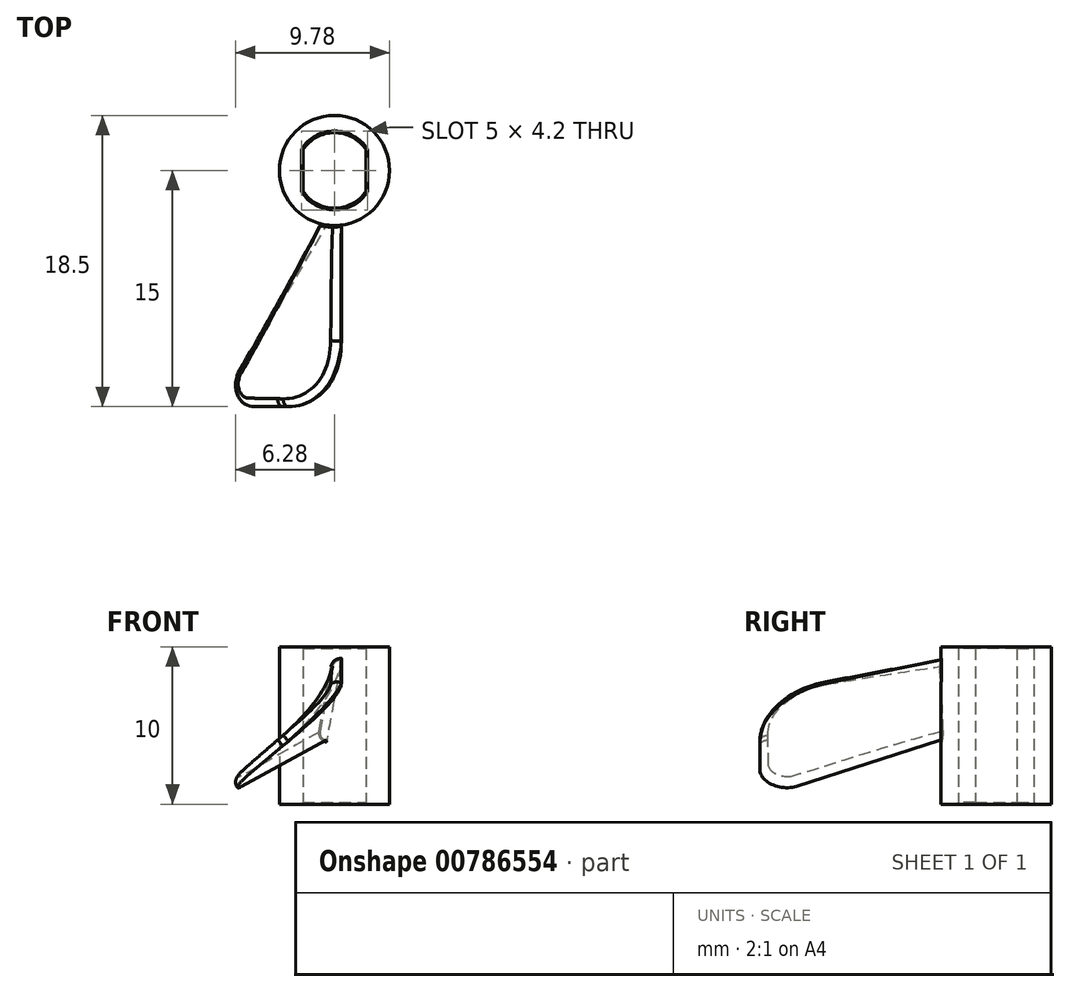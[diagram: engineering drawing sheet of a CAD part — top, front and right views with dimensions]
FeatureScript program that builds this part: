
annotation { "Feature Type Name" : "Feature", "Feature Type Description" : "" }
export const myFeature = defineFeature(function(context is Context, id is Id, definition is map)
    precondition{}
    {
        {
            var Q0;
            Q0=qCreatedBy(makeId("Top.planeOp"),FACE);
            var sketch = newSketch(context, id + "F0", { "sketchPlane" : qUnion([Q0])});
            skCircle(sketch, "E0", {"center": v(0, 0) * mm, "radius": 2.4 * mm});
            skLineSegment(sketch, "E1", {"start": v(-2, 1.33) * mm, "end": v(2, 1.33) * mm});
            skLineSegment(sketch, "E2", {"start": v(-2, -1.33) * mm, "end": v(2, -1.33) * mm});
            skLineSegment(sketch, "E3", {"start": v(-2, 1.33) * mm, "end": v(-2, -1.33) * mm});
            skLineSegment(sketch, "E4", {"start": v(2, 1.33) * mm, "end": v(2, -1.33) * mm});
            skCircle(sketch, "E5", {"center": v(0, 0) * mm, "radius": 3.5 * mm});
            skSolve(sketch);
        }
        {
            var Q0;
            Q0=makeQuery(id+"F0.imprint","IMPRINT",FACE,{"disambiguationData":[TD([[makeQuery(id+"F0.imprint","IMPRINT",EDGE,{"derivedFrom":sQuery(id+"F0.wireOp",EDGE,"E5")}),1.0]])]});
            var Q1;
            {var subQ0=sQuery(id+"F0.wireOp",EDGE,"E4");Q1=makeQuery(id+"F0.imprint","IMPRINT",FACE,{"disambiguationData":[TD([[makeQuery(id+"F0.imprint","IMPRINT",EDGE,{"derivedFrom":subQ0}),1.0]])]});}
            var Q2;
            {var subQ0=sQuery(id+"F0.wireOp",EDGE,"E3");Q2=makeQuery(id+"F0.imprint","IMPRINT",FACE,{"disambiguationData":[TD([[makeQuery(id+"F0.imprint","IMPRINT",EDGE,{"derivedFrom":subQ0}),-1.0]])]});}
            extrude(context, id + "F1", {"entities" : qUnion([Q0, Q1, Q2]), "depth" : 10 * mm, "offsetDistance" : 25 * mm});
        }
        {
            var Q0;
            Q0=qCreatedBy(makeId("Front.planeOp"),FACE);
            cPlane(context, id + "F2", {"entities" : qUnion([Q0]), "cplaneType" : CPlaneType.OFFSET, "offset" : 15 * mm, "width" : 150 * mm, "height" : 150 * mm});
        }
        {
            var Q0;
            Q0=qCreatedBy(id+"F2.planeOp",FACE);
            var sketch = newSketch(context, id + "F3", { "sketchPlane" : qUnion([Q0])});
            skLineSegment(sketch, "E6", {"start": v(-7.23, 10) * mm, "end": v(-7.23, 0) * mm, "construction": true});
            skLineSegment(sketch, "E7", {"start": v(-7.23, 0.38) * mm, "end": v(0.43, 6.81) * mm});
            skLineSegment(sketch, "E8", {"start": v(0.43, 6.81) * mm, "end": v(0.1, 7.2) * mm});
            skLineSegment(sketch, "E9", {"start": v(0.1, 7.2) * mm, "end": v(-7.55, 0.77) * mm});
            skLineSegment(sketch, "E10", {"start": v(-7.55, 0.77) * mm, "end": v(-7.23, 0.38) * mm});
            skSolve(sketch);
        }
        {
            var Q0;
            Q0=qCreatedBy(makeId("Front.planeOp"),FACE);
            cPlane(context, id + "F4", {"entities" : qUnion([Q0]), "cplaneType" : CPlaneType.OFFSET, "offset" : 2.6 * mm, "width" : 150 * mm, "height" : 150 * mm});
        }
        {
            var Q0;
            Q0=qCreatedBy(id+"F4.planeOp",FACE);
            var sketch = newSketch(context, id + "F5", { "sketchPlane" : qUnion([Q0])});
            skLineSegment(sketch, "E11", {"start": v(-0.48, 0) * mm, "end": v(-0.48, 9) * mm, "construction": true});
            skLineSegment(sketch, "E12", {"start": v(-0.48, 4.4) * mm, "end": v(-0.04, 9.39) * mm});
            skLineSegment(sketch, "E13", {"start": v(-0.04, 9.39) * mm, "end": v(0.45, 9.35) * mm});
            skLineSegment(sketch, "E14", {"start": v(0.45, 9.35) * mm, "end": v(0.02, 4.37) * mm});
            skLineSegment(sketch, "E15", {"start": v(0.02, 4.37) * mm, "end": v(-0.48, 4.4) * mm});
            skSolve(sketch);
        }
        {
            var Q1;
            Q1=qSketchRegion(id+"F3",true);
            var Q2;
            Q2=qSketchRegion(id+"F5",true);
            loft(context, id + "F6", {"operationType" : NewBodyOperationType.ADD, "sheetProfilesArray" : [{ "sheetProfileEntities" : qUnion([Q1]) }, { "sheetProfileEntities" : qUnion([Q2]) }]});
        }
        {
            var Q0;
            Q0=makeQuery(id+"F26cwcx8InL0C1a_1.2.F6.opLoft","MID_CAP_EDGE",EDGE,{"disambiguationData":[OSD([sQuery(id+"F3.wireOp",EDGE,"E7"),sQuery(id+"F3.wireOp",EDGE,"E8"),sQuery(id+"F3.wireOp",EDGE,"E9")])],"capPos":0.0});
            var Q1;
            Q1=makeQuery(id+"F6.opLoft","MID_CAP_EDGE",EDGE,{"disambiguationData":[OSD([sQuery(id+"F3.wireOp",EDGE,"E7"),sQuery(id+"F3.wireOp",EDGE,"E8"),sQuery(id+"F3.wireOp",EDGE,"E9")])],"capPos":0.0});
            var Q2;
            Q2=makeQuery(id+"F26cwcx8InL0C1a_1.1.F6.opLoft","MID_CAP_EDGE",EDGE,{"disambiguationData":[OSD([sQuery(id+"F3.wireOp",EDGE,"E7"),sQuery(id+"F3.wireOp",EDGE,"E8"),sQuery(id+"F3.wireOp",EDGE,"E9")])],"capPos":0.0});
            var Q3;
            Q3=makeQuery(id+"F26cwcx8InL0C1a_1.4.F6.opLoft","MID_CAP_EDGE",EDGE,{"disambiguationData":[OSD([sQuery(id+"F3.wireOp",EDGE,"E7"),sQuery(id+"F3.wireOp",EDGE,"E8"),sQuery(id+"F3.wireOp",EDGE,"E9")])],"capPos":0.0});
            var Q4;
            Q4=makeQuery(id+"F26cwcx8InL0C1a_1.3.F6.opLoft","MID_CAP_EDGE",EDGE,{"disambiguationData":[OSD([sQuery(id+"F3.wireOp",EDGE,"E7"),sQuery(id+"F3.wireOp",EDGE,"E8"),sQuery(id+"F3.wireOp",EDGE,"E9")])],"capPos":0.0});
            fillet(context, id + "F7", {"entities" : qUnion([Q0, Q1, Q2, Q3, Q4]), "radius" : 5 * mm, "tangentPropagation" : true, "allowEdgeOverflow" : false});
        }
        {
            var Q0;
            Q0=makeQuery(id+"F6.opLoft","MID_CAP_EDGE",EDGE,{"disambiguationData":[OSD([sQuery(id+"F3.wireOp",EDGE,"E7"),sQuery(id+"F3.wireOp",EDGE,"E9"),sQuery(id+"F3.wireOp",EDGE,"E10")])],"capPos":0.0});
            var Q1;
            Q1=makeQuery(id+"F26cwcx8InL0C1a_1.2.F6.opLoft","MID_CAP_EDGE",EDGE,{"disambiguationData":[OSD([sQuery(id+"F3.wireOp",EDGE,"E7"),sQuery(id+"F3.wireOp",EDGE,"E9"),sQuery(id+"F3.wireOp",EDGE,"E10")])],"capPos":0.0});
            var Q2;
            Q2=makeQuery(id+"F26cwcx8InL0C1a_1.1.F6.opLoft","MID_CAP_EDGE",EDGE,{"disambiguationData":[OSD([sQuery(id+"F3.wireOp",EDGE,"E7"),sQuery(id+"F3.wireOp",EDGE,"E9"),sQuery(id+"F3.wireOp",EDGE,"E10")])],"capPos":0.0});
            var Q3;
            Q3=makeQuery(id+"F26cwcx8InL0C1a_1.4.F6.opLoft","MID_CAP_EDGE",EDGE,{"disambiguationData":[OSD([sQuery(id+"F3.wireOp",EDGE,"E7"),sQuery(id+"F3.wireOp",EDGE,"E9"),sQuery(id+"F3.wireOp",EDGE,"E10")])],"capPos":0.0});
            var Q4;
            Q4=makeQuery(id+"F26cwcx8InL0C1a_1.3.F6.opLoft","MID_CAP_EDGE",EDGE,{"disambiguationData":[OSD([sQuery(id+"F3.wireOp",EDGE,"E7"),sQuery(id+"F3.wireOp",EDGE,"E9"),sQuery(id+"F3.wireOp",EDGE,"E10")])],"capPos":0.0});
            fillet(context, id + "F8", {"entities" : qUnion([Q0, Q1, Q2, Q3, Q4]), "radius" : 1.5 * mm, "tangentPropagation" : true, "allowEdgeOverflow" : false});
        }
        {
            var Q0;
            Q0=makeQuery(id+"F26cwcx8InL0C1a_1.1.F6.opLoft","SWEPT_EDGE",EDGE,{"disambiguationData":[OSD([sQuery(id+"F3.wireOp",EDGE,"E8"),sQuery(id+"F3.wireOp",EDGE,"E9"),sQuery(id+"F5.wireOp",EDGE,"E12"),sQuery(id+"F5.wireOp",EDGE,"E13")])]});
            var Q1;
            Q1=makeQuery(id+"F6.opLoft","SWEPT_EDGE",EDGE,{"disambiguationData":[OSD([sQuery(id+"F3.wireOp",EDGE,"E8"),sQuery(id+"F3.wireOp",EDGE,"E9"),sQuery(id+"F5.wireOp",EDGE,"E12"),sQuery(id+"F5.wireOp",EDGE,"E13")])]});
            var Q2;
            Q2=makeQuery(id+"F26cwcx8InL0C1a_1.2.F6.opLoft","SWEPT_EDGE",EDGE,{"disambiguationData":[OSD([sQuery(id+"F3.wireOp",EDGE,"E8"),sQuery(id+"F3.wireOp",EDGE,"E9"),sQuery(id+"F5.wireOp",EDGE,"E12"),sQuery(id+"F5.wireOp",EDGE,"E13")])]});
            var Q3;
            Q3=makeQuery(id+"F26cwcx8InL0C1a_1.3.F6.opLoft","SWEPT_EDGE",EDGE,{"disambiguationData":[OSD([sQuery(id+"F3.wireOp",EDGE,"E8"),sQuery(id+"F3.wireOp",EDGE,"E9"),sQuery(id+"F5.wireOp",EDGE,"E12"),sQuery(id+"F5.wireOp",EDGE,"E13")])]});
            var Q4;
            Q4=makeQuery(id+"F26cwcx8InL0C1a_1.4.F6.opLoft","SWEPT_EDGE",EDGE,{"disambiguationData":[OSD([sQuery(id+"F3.wireOp",EDGE,"E8"),sQuery(id+"F3.wireOp",EDGE,"E9"),sQuery(id+"F5.wireOp",EDGE,"E12"),sQuery(id+"F5.wireOp",EDGE,"E13")])]});
            fillet(context, id + "F9", {"entities" : qUnion([Q0, Q1, Q2, Q3, Q4]), "radius" : 0.5 * mm, "tangentPropagation" : true, "allowEdgeOverflow" : false});
        }
        {
            var Q0;
            Q0=makeQuery(id+"F9.opFillet","BLEND_EDGE",EDGE,{"blendedFrom":[makeQuery(id+"F26cwcx8InL0C1a_1.1.F6.opLoft","SWEPT_EDGE",EDGE,{"disambiguationData":[OSD([sQuery(id+"F3.wireOp",EDGE,"E8"),sQuery(id+"F3.wireOp",EDGE,"E9"),sQuery(id+"F5.wireOp",EDGE,"E12"),sQuery(id+"F5.wireOp",EDGE,"E13")])]}),makeQuery(id+"F1.opExtrude","SWEPT_FACE",FACE,{"disambiguationData":[OSD([sQuery(id+"F0.wireOp",EDGE,"E5")])]})],"blendedInto":[makeQuery(id+"F1.opExtrude","SWEPT_FACE",FACE,{"disambiguationData":[OSD([sQuery(id+"F0.wireOp",EDGE,"E5")])]})]});
            var Q1;
            Q1=makeQuery(id+"F6.boolean.opBoolean","INTERSECT",EDGE,{"derivedFrom":[makeQuery(id+"F1.opExtrude","SWEPT_FACE",FACE,{"disambiguationData":[OSD([sQuery(id+"F0.wireOp",EDGE,"E5")])]}),makeQuery(id+"F6.opLoft","SWEPT_FACE",FACE,{"disambiguationData":[OSD([sQuery(id+"F3.wireOp",EDGE,"E8"),sQuery(id+"F3.wireOp",EDGE,"E9"),sQuery(id+"F3.wireOp",EDGE,"E10"),sQuery(id+"F5.wireOp",EDGE,"E12"),sQuery(id+"F5.wireOp",EDGE,"E13"),sQuery(id+"F5.wireOp",EDGE,"E15")])]})]});
            var Q2;
            Q2=makeQuery(id+"F26cwcx8InL0C1a_1.2.F6.boolean.opBoolean","INTERSECT",EDGE,{"derivedFrom":[makeQuery(id+"F1.opExtrude","SWEPT_FACE",FACE,{"disambiguationData":[OSD([sQuery(id+"F0.wireOp",EDGE,"E5")])]}),makeQuery(id+"F26cwcx8InL0C1a_1.2.F6.opLoft","SWEPT_FACE",FACE,{"disambiguationData":[OSD([sQuery(id+"F3.wireOp",EDGE,"E8"),sQuery(id+"F3.wireOp",EDGE,"E9"),sQuery(id+"F3.wireOp",EDGE,"E10"),sQuery(id+"F5.wireOp",EDGE,"E12"),sQuery(id+"F5.wireOp",EDGE,"E13"),sQuery(id+"F5.wireOp",EDGE,"E15")])]})]});
            var Q3;
            Q3=makeQuery(id+"F26cwcx8InL0C1a_1.4.F6.boolean.opBoolean","INTERSECT",EDGE,{"derivedFrom":[makeQuery(id+"F1.opExtrude","SWEPT_FACE",FACE,{"disambiguationData":[OSD([sQuery(id+"F0.wireOp",EDGE,"E5")])]}),makeQuery(id+"F26cwcx8InL0C1a_1.4.F6.opLoft","SWEPT_FACE",FACE,{"disambiguationData":[OSD([sQuery(id+"F3.wireOp",EDGE,"E8"),sQuery(id+"F3.wireOp",EDGE,"E9"),sQuery(id+"F3.wireOp",EDGE,"E10"),sQuery(id+"F5.wireOp",EDGE,"E12"),sQuery(id+"F5.wireOp",EDGE,"E13"),sQuery(id+"F5.wireOp",EDGE,"E15")])]})]});
            var Q4;
            Q4=makeQuery(id+"F26cwcx8InL0C1a_1.3.F6.boolean.opBoolean","INTERSECT",EDGE,{"derivedFrom":[makeQuery(id+"F1.opExtrude","SWEPT_FACE",FACE,{"disambiguationData":[OSD([sQuery(id+"F0.wireOp",EDGE,"E5")])]}),makeQuery(id+"F26cwcx8InL0C1a_1.3.F6.opLoft","SWEPT_FACE",FACE,{"disambiguationData":[OSD([sQuery(id+"F3.wireOp",EDGE,"E8"),sQuery(id+"F3.wireOp",EDGE,"E9"),sQuery(id+"F3.wireOp",EDGE,"E10"),sQuery(id+"F5.wireOp",EDGE,"E12"),sQuery(id+"F5.wireOp",EDGE,"E13"),sQuery(id+"F5.wireOp",EDGE,"E15")])]})]});
            fillet(context, id + "F10", {"entities" : qUnion([Q0, Q1, Q2, Q3, Q4]), "radius" : 0.1 * mm, "tangentPropagation" : true, "allowEdgeOverflow" : false});
        }
        {
            var Q0;
            {var subQ0=sQuery(id+"F0.wireOp",EDGE,"E1");var subQ1=sQuery(id+"F0.wireOp",EDGE,"E0");Q0=makeQuery(id+"F1.opExtrude","CAP_EDGE",EDGE,{"disambiguationData":[OSD([subQ1]),TDD([makeQuery(id+"F0.imprint","IMPRINT",EDGE,{"disambiguationData":[TD([[makeQuery(id+"F0.imprint","INTERSECT",VERTEX,{"derivedFrom":[subQ1,subQ0,sQuery(id+"F0.wireOp",EDGE,"E3")]}),1.0]])],"derivedFrom":subQ1})])],"isStart":false});}
            var Q1;
            Q1=makeQuery(id+"F1.opExtrude","CAP_EDGE",EDGE,{"disambiguationData":[OSD([sQuery(id+"F0.wireOp",EDGE,"E3")])],"isStart":false});
            var Q2;
            {var subQ0=sQuery(id+"F0.wireOp",EDGE,"E2");var subQ1=sQuery(id+"F0.wireOp",EDGE,"E0");Q2=makeQuery(id+"F1.opExtrude","CAP_EDGE",EDGE,{"disambiguationData":[OSD([subQ1]),TDD([makeQuery(id+"F0.imprint","IMPRINT",EDGE,{"disambiguationData":[TD([[makeQuery(id+"F0.imprint","INTERSECT",VERTEX,{"derivedFrom":[subQ1,subQ0,sQuery(id+"F0.wireOp",EDGE,"E3")]}),-1.0]])],"derivedFrom":subQ1})])],"isStart":false});}
            var Q3;
            Q3=makeQuery(id+"F1.opExtrude","CAP_EDGE",EDGE,{"disambiguationData":[OSD([sQuery(id+"F0.wireOp",EDGE,"E4")])],"isStart":false});
            var Q4;
            Q4=makeQuery(id+"F1.opExtrude","CAP_EDGE",EDGE,{"disambiguationData":[OSD([sQuery(id+"F0.wireOp",EDGE,"E4")])],"isStart":true});
            var Q5;
            {var subQ0=sQuery(id+"F0.wireOp",EDGE,"E2");var subQ1=sQuery(id+"F0.wireOp",EDGE,"E0");Q5=makeQuery(id+"F1.opExtrude","CAP_EDGE",EDGE,{"disambiguationData":[OSD([subQ1]),TDD([makeQuery(id+"F0.imprint","IMPRINT",EDGE,{"disambiguationData":[TD([[makeQuery(id+"F0.imprint","INTERSECT",VERTEX,{"derivedFrom":[subQ1,subQ0,sQuery(id+"F0.wireOp",EDGE,"E3")]}),-1.0]])],"derivedFrom":subQ1})])],"isStart":true});}
            var Q6;
            Q6=makeQuery(id+"F1.opExtrude","CAP_EDGE",EDGE,{"disambiguationData":[OSD([sQuery(id+"F0.wireOp",EDGE,"E3")])],"isStart":true});
            var Q7;
            {var subQ0=sQuery(id+"F0.wireOp",EDGE,"E1");var subQ1=sQuery(id+"F0.wireOp",EDGE,"E0");Q7=makeQuery(id+"F1.opExtrude","CAP_EDGE",EDGE,{"disambiguationData":[OSD([subQ1]),TDD([makeQuery(id+"F0.imprint","IMPRINT",EDGE,{"disambiguationData":[TD([[makeQuery(id+"F0.imprint","INTERSECT",VERTEX,{"derivedFrom":[subQ1,subQ0,sQuery(id+"F0.wireOp",EDGE,"E3")]}),1.0]])],"derivedFrom":subQ1})])],"isStart":true});}
            chamfer(context, id + "F11", {"entities" : qUnion([Q0, Q1, Q2, Q3, Q4, Q5, Q6, Q7]), "width" : 0.1 * mm, "tangentPropagation" : true});
        }
    });
